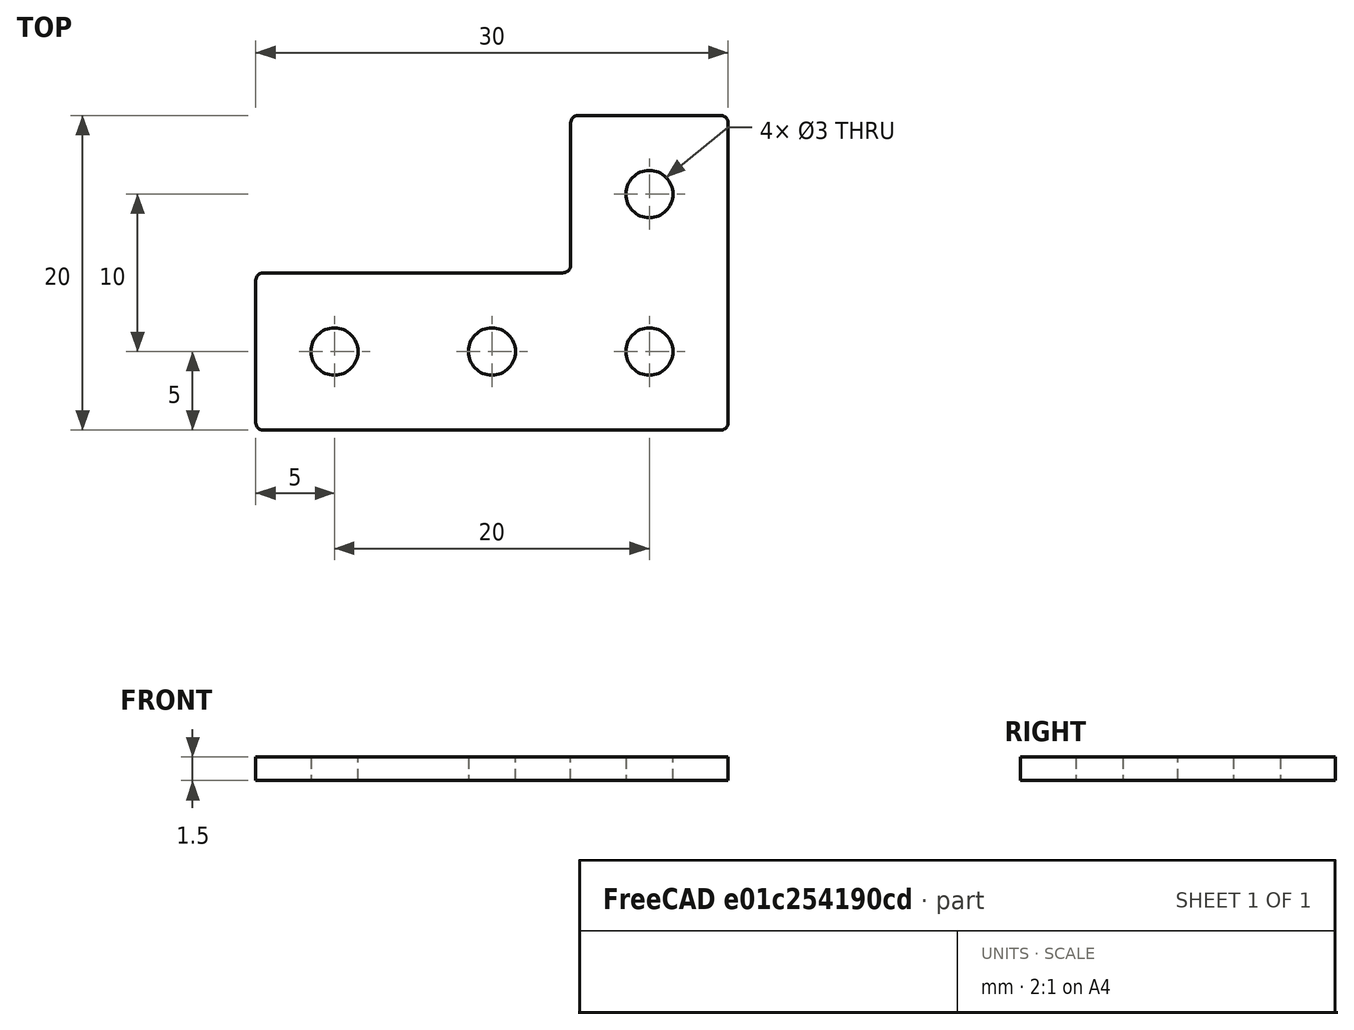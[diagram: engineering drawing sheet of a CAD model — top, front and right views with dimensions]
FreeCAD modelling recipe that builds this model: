
FCSTD DOCUMENT  (FreeCAD 0.18R16146 (Git))
Label: makerbeam_bracket_90degree
License: All rights reserved
LicenseURL: http://en.wikipedia.org/wiki/All_rights_reserved
objects: Sketcher::SketchObject×1, PartDesign::Pad×1, PartDesign::Fillet×1, PartDesign::Body×1
note: 5 computed .brp shape members not serialized (recipe doc carries the construction recipe); baked Part::Feature solids carry a one-line shape summary decoded from their .brp

FEATURE [Sketcher::SketchObject] Sketch
  MapMode = 5
  Support = -> [XY_Plane]
  sketch-geometry (10):
    g0: Circle CenterX=-20 CenterY=0 CenterZ=0 NormalX=0 NormalY=0 NormalZ=1 AngleXU=0 Radius=1.5
    g1: Circle CenterX=-10 CenterY=0 CenterZ=0 NormalX=0 NormalY=0 NormalZ=1 AngleXU=0 Radius=1.5
    g2: Circle CenterX=0 CenterY=0 CenterZ=0 NormalX=0 NormalY=0 NormalZ=1 AngleXU=0 Radius=1.5
    g3: Circle CenterX=0 CenterY=10 CenterZ=0 NormalX=0 NormalY=0 NormalZ=1 AngleXU=0 Radius=1.5
    g4: LineSegment StartX=-25 StartY=-5 StartZ=0 EndX=5 EndY=-5 EndZ=0
    g5: LineSegment StartX=5 StartY=-5 StartZ=0 EndX=5 EndY=15 EndZ=0
    g6: LineSegment StartX=5 StartY=15 StartZ=0 EndX=-5 EndY=15 EndZ=0
    g7: LineSegment StartX=-5 StartY=15 StartZ=0 EndX=-5 EndY=5 EndZ=0
    g8: LineSegment StartX=-5 StartY=5 StartZ=0 EndX=-25 EndY=5 EndZ=0
    g9: LineSegment StartX=-25 StartY=5 StartZ=0 EndX=-25 EndY=-5 EndZ=0
  constraints (16):
    c: Radius(g0) = 1.5
    c: Equal(g0,g1) = 1.5
    c: Equal(g0,g2) = 1.5
    c: Equal(g0,g3) = 1.5
    c: Horizontal(g4)
    c: Coincident(g4,g5)
    c: Vertical(g5)
    c: Coincident(g5,g6)
    c: Horizontal(g6)
    c: Coincident(g6,g7)
    c: Vertical(g7)
    c: Coincident(g7,g8)
    c: Horizontal(g8)
    c: Coincident(g8,g9)
    c: Coincident(g9,g4)
    c: Vertical(g9)
FEATURE [PartDesign::Pad] Pad
  Length = 1.5
  Length2 = 100
  Profile = -> Sketch
  Type = 0
FEATURE [PartDesign::Fillet] Fillet
  Base = -> Pad [Edge2,Edge14,Edge5,Edge8,Edge11,Edge1]
  BaseFeature = -> Pad
  Radius = 0.5
FEATURE [PartDesign::Body] Body  label="makerbeam_bracket_90degree"
  Group = -> [Sketch,Pad,Fillet]
  Origin = -> Origin
  Tip = -> Fillet
